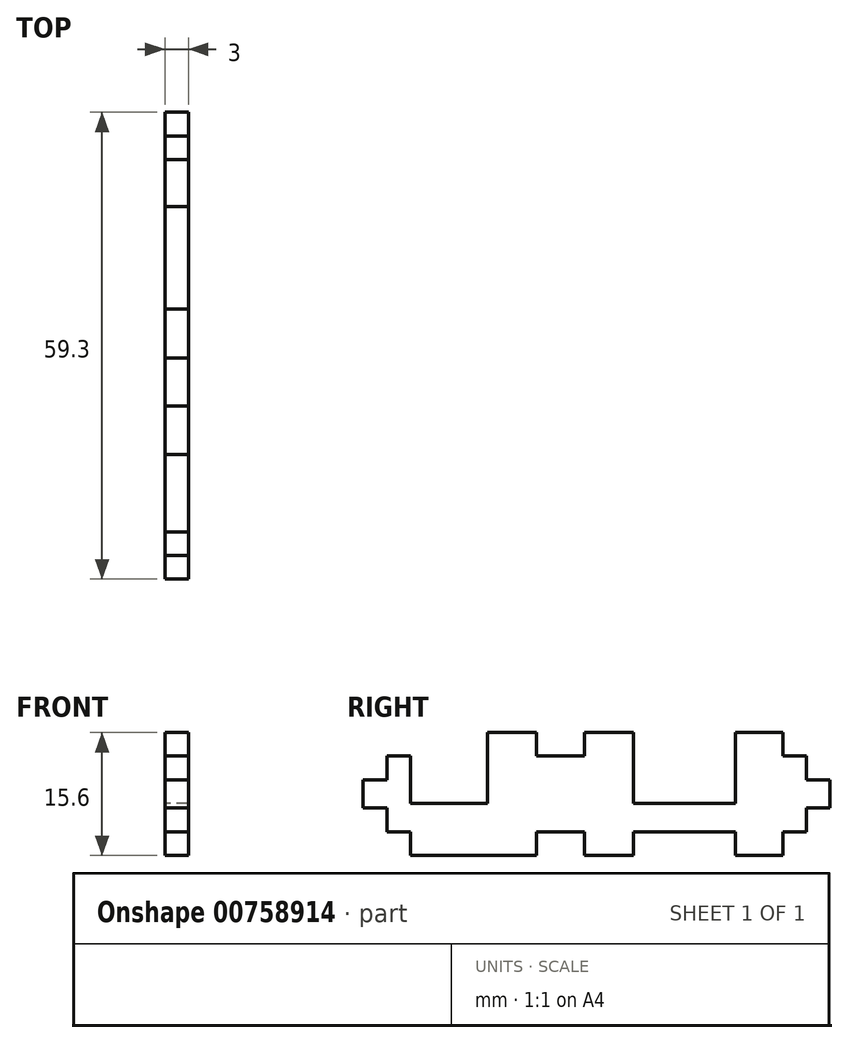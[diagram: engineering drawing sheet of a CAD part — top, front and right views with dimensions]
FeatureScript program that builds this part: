
annotation { "Feature Type Name" : "Feature", "Feature Type Description" : "" }
export const myFeature = defineFeature(function(context is Context, id is Id, definition is map)
    precondition{}
    {
        {
            var Q0;
            Q0=qCreatedBy(makeId("Right.planeOp"),FACE);
            var sketch = newSketch(context, id + "F0", { "sketchPlane" : qUnion([Q0])});
            skLineSegment(sketch, "E0", {"start": v(0, -6) * mm, "end": v(3, -6) * mm});
            skLineSegment(sketch, "E1", {"start": v(3, -6) * mm, "end": v(3, -3) * mm});
            skLineSegment(sketch, "E2", {"start": v(3, -3) * mm, "end": v(6, -3) * mm});
            skLineSegment(sketch, "E3", {"start": v(6, -3) * mm, "end": v(6, -9) * mm});
            skLineSegment(sketch, "E4", {"start": v(6, -9) * mm, "end": v(15.8, -9) * mm});
            skLineSegment(sketch, "E5", {"start": v(15.8, -9) * mm, "end": v(15.8, 0) * mm});
            skLineSegment(sketch, "E6", {"start": v(15.8, 0) * mm, "end": v(22, 0) * mm});
            skLineSegment(sketch, "E7", {"start": v(22, 0) * mm, "end": v(22, -3) * mm});
            skLineSegment(sketch, "E8", {"start": v(22, -3) * mm, "end": v(28.1, -3) * mm});
            skLineSegment(sketch, "E9", {"start": v(28.1, -3) * mm, "end": v(28.1, 0) * mm});
            skLineSegment(sketch, "E10", {"start": v(28.1, 0) * mm, "end": v(34.3, 0) * mm});
            skLineSegment(sketch, "E11", {"start": v(34.3, 0) * mm, "end": v(34.3, -9) * mm});
            skLineSegment(sketch, "E12", {"start": v(34.3, -9) * mm, "end": v(47.3, -9) * mm});
            skLineSegment(sketch, "E13", {"start": v(47.3, -9) * mm, "end": v(47.3, 0) * mm});
            skLineSegment(sketch, "E14", {"start": v(47.3, 0) * mm, "end": v(53.3, 0) * mm});
            skLineSegment(sketch, "E15", {"start": v(53.3, 0) * mm, "end": v(53.3, -3) * mm});
            skLineSegment(sketch, "E16", {"start": v(53.3, -3) * mm, "end": v(56.3, -3) * mm});
            skLineSegment(sketch, "E17", {"start": v(56.3, -3) * mm, "end": v(56.3, -6) * mm});
            skLineSegment(sketch, "E18", {"start": v(56.3, -6) * mm, "end": v(59.3, -6) * mm});
            skLineSegment(sketch, "E19", {"start": v(59.3, -6) * mm, "end": v(59.3, -9.6) * mm});
            skLineSegment(sketch, "E20", {"start": v(59.3, -9.6) * mm, "end": v(56.3, -9.6) * mm});
            skLineSegment(sketch, "E21", {"start": v(56.3, -9.6) * mm, "end": v(56.3, -12.6) * mm});
            skLineSegment(sketch, "E22", {"start": v(56.3, -12.6) * mm, "end": v(53.3, -12.6) * mm});
            skLineSegment(sketch, "E23", {"start": v(53.3, -12.6) * mm, "end": v(53.3, -15.6) * mm});
            skLineSegment(sketch, "E24", {"start": v(53.3, -15.6) * mm, "end": v(47.3, -15.6) * mm});
            skLineSegment(sketch, "E25", {"start": v(47.3, -15.6) * mm, "end": v(47.3, -12.6) * mm});
            skLineSegment(sketch, "E26", {"start": v(47.3, -12.6) * mm, "end": v(34.3, -12.6) * mm});
            skLineSegment(sketch, "E27", {"start": v(34.3, -12.6) * mm, "end": v(34.3, -15.6) * mm});
            skLineSegment(sketch, "E28", {"start": v(34.3, -15.6) * mm, "end": v(28.1, -15.6) * mm});
            skLineSegment(sketch, "E29", {"start": v(28.1, -15.6) * mm, "end": v(28.1, -12.6) * mm});
            skLineSegment(sketch, "E30", {"start": v(28.1, -12.6) * mm, "end": v(22, -12.6) * mm});
            skLineSegment(sketch, "E31", {"start": v(22, -12.6) * mm, "end": v(22, -15.6) * mm});
            skLineSegment(sketch, "E32", {"start": v(22, -15.6) * mm, "end": v(6, -15.6) * mm});
            skLineSegment(sketch, "E33", {"start": v(6, -15.6) * mm, "end": v(6, -12.6) * mm});
            skLineSegment(sketch, "E34", {"start": v(6, -12.6) * mm, "end": v(3, -12.6) * mm});
            skLineSegment(sketch, "E35", {"start": v(0, -6) * mm, "end": v(0, -9.6) * mm});
            skLineSegment(sketch, "E36", {"start": v(0, -9.6) * mm, "end": v(3, -9.6) * mm});
            skLineSegment(sketch, "E37", {"start": v(3, -9.6) * mm, "end": v(3, -12.6) * mm});
            skSolve(sketch);
        }
        {
            var Q0;
            Q0 = qSketchRegion(id + "F0", true);
            extrude(context, id + "F1", {"entities" : qUnion([Q0]), "depth" : 3 * mm, "offsetDistance" : 25 * mm});
        }
    });
